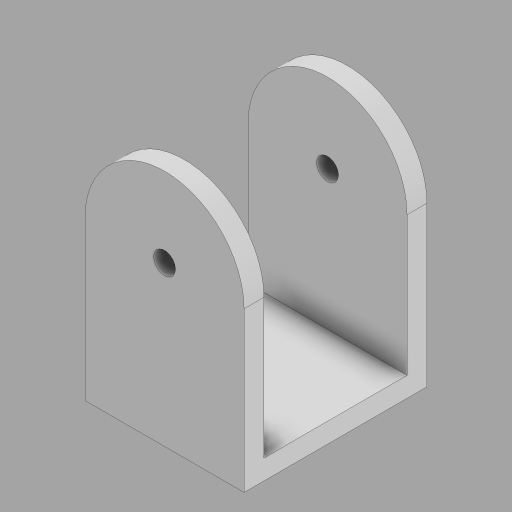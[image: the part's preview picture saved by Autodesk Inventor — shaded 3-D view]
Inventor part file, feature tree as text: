
AUTODESK INVENTOR PART (.ipt)
format: ipt  version: 2023.2 (Build 272271030, 271C)  size: 275,968 bytes
history: native  units: mm
features: extrude x3, sketch x2, fillet x1, projected_geometry x1
ambient origin geometry x8: Origin, YZ Plane, XZ Plane, XY Plane, X Axis, Y Axis, Z Axis, Center Point
bodies: Solid1 (feature_tree)
feature tree (7):
  sketch  "Sketch1"  dims[d1=40.0mm d2=46.0mm]
  extrude  "Extrusion1"  Depth=46.0mm
  extrude  "Extrusion2"  Depth=5.0mm
  fillet  "Fillet1"  Radius=5.0mm
  extrude  "Extrusion3"  Depth=20.0mm TaperAngle=0.0deg
  sketch  "Sketch2"  dims[d3=5.0mm d4=5.0mm d5=5.0mm d6=0.0mm d7=60.0mm d8=0.0mm d9=20.0mm d10=5.5mm d11=600.0mm d12=0.0mm]
  projected_geometry  "Projected Loop1"
